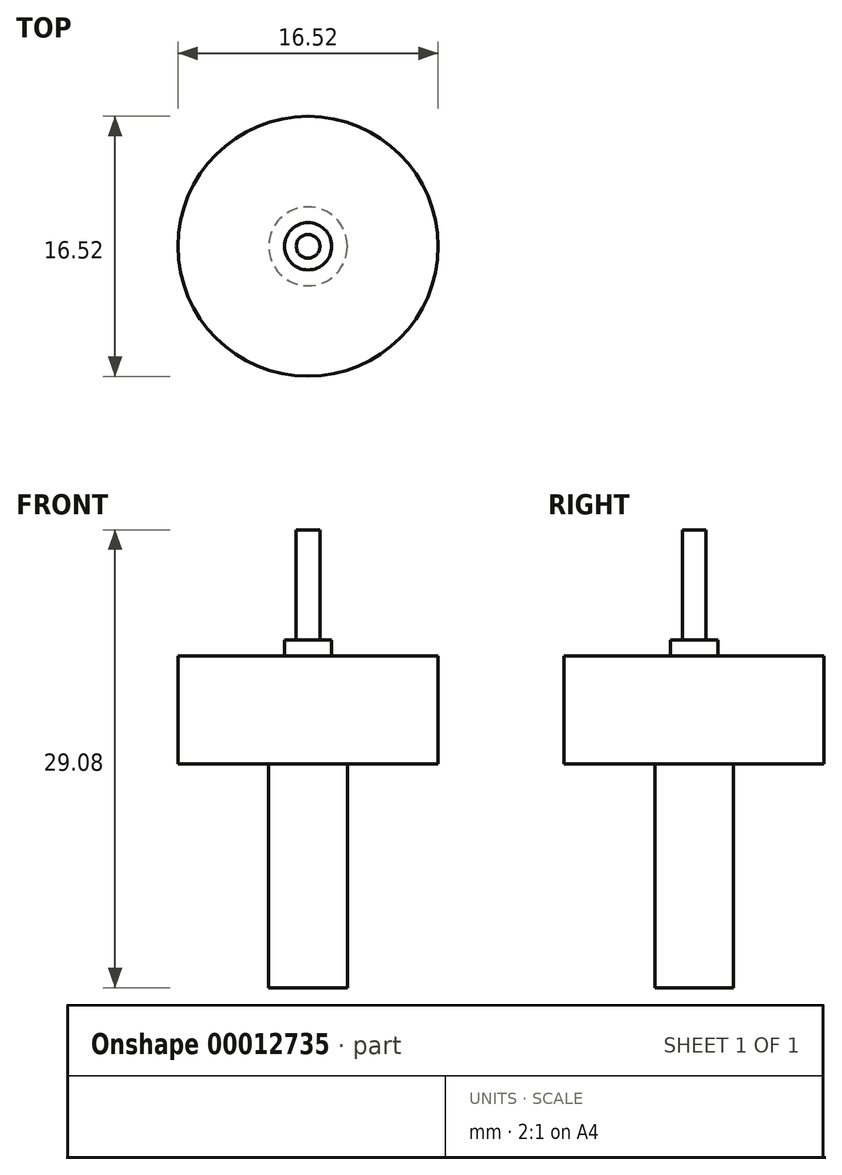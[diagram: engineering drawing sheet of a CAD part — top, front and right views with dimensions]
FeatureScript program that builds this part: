
annotation { "Feature Type Name" : "Feature", "Feature Type Description" : "" }
export const myFeature = defineFeature(function(context is Context, id is Id, definition is map)
    precondition{}
    {
        {
            var Q0;
            Q0=qCreatedBy(makeId("Top.planeOp"),FACE);
            var sketch = newSketch(context, id + "F0", { "sketchPlane" : qUnion([Q0])});
            skCircle(sketch, "E0", {"center": v(0, 0) * mm, "radius": 8.26 * mm});
            skCircle(sketch, "E1", {"center": v(0, 0) * mm, "radius": 2.5 * mm});
            skCircle(sketch, "E2", {"center": v(0, 0) * mm, "radius": 0.75 * mm});
            skSolve(sketch);
        }
        {
            var Q0;
            Q0=makeQuery(id+"F0.imprint","IMPRINT",FACE,{"disambiguationData":[TD([[makeQuery(id+"F0.imprint","IMPRINT",EDGE,{"derivedFrom":sQuery(id+"F0.wireOp",EDGE,"E0")}),1.0]])]});
            var Q1;
            Q1=makeQuery(id+"F0.imprint","IMPRINT",FACE,{"disambiguationData":[TD([[makeQuery(id+"F0.imprint","IMPRINT",EDGE,{"derivedFrom":sQuery(id+"F0.wireOp",EDGE,"E1")}),1.0]])]});
            var Q2;
            Q2=makeQuery(id+"F0.imprint","IMPRINT",FACE,{"disambiguationData":[TD([[makeQuery(id+"F0.imprint","IMPRINT",EDGE,{"derivedFrom":sQuery(id+"F0.wireOp",EDGE,"E2")}),1.0]])]});
            extrude(context, id + "F1", {"entities" : qUnion([Q0, Q1, Q2]), "depth" : 6.86 * mm});
        }
        {
            var Q0;
            Q0=makeQuery(id+"F0.imprint","IMPRINT",FACE,{"disambiguationData":[TD([[makeQuery(id+"F0.imprint","IMPRINT",EDGE,{"derivedFrom":sQuery(id+"F0.wireOp",EDGE,"E1")}),1.0]])]});
            var Q1;
            Q1=makeQuery(id+"F0.imprint","IMPRINT",FACE,{"disambiguationData":[TD([[makeQuery(id+"F0.imprint","IMPRINT",EDGE,{"derivedFrom":sQuery(id+"F0.wireOp",EDGE,"E2")}),1.0]])]});
            extrude(context, id + "F2", {"entities" : qUnion([Q0, Q1]), "operationType" : NewBodyOperationType.ADD, "oppositeDirection" : true, "depth" : 14.22 * mm});
        }
        {
            var Q0;
            Q0=makeQuery(id+"F1.opExtrude","CAP_FACE",FACE,{"disambiguationData":[OSD([sQuery(id+"F0.wireOp",EDGE,"E0")])],"isStart":false});
            var sketch = newSketch(context, id + "F3", { "sketchPlane" : qUnion([Q0])});
            skCircle(sketch, "E3", {"center": v(0, 0) * mm, "radius": 1.5 * mm});
            skCircle(sketch, "E4", {"center": v(0, 0) * mm, "radius": 0.75 * mm});
            skSolve(sketch);
        }
        {
            var Q0;
            Q0=makeQuery(id+"F3.imprint","IMPRINT",FACE,{"disambiguationData":[TD([[makeQuery(id+"F3.imprint","IMPRINT",EDGE,{"derivedFrom":sQuery(id+"F3.wireOp",EDGE,"E4")}),1.0]])]});
            extrude(context, id + "F4", {"entities" : qUnion([Q0]), "operationType" : NewBodyOperationType.ADD, "depth" : 8 * mm});
        }
        {
            var Q0;
            Q0=makeQuery(id+"F3.imprint","IMPRINT",FACE,{"disambiguationData":[TD([[makeQuery(id+"F3.imprint","IMPRINT",EDGE,{"derivedFrom":sQuery(id+"F3.wireOp",EDGE,"E3")}),1.0]])]});
            extrude(context, id + "F5", {"entities" : qUnion([Q0]), "operationType" : NewBodyOperationType.ADD, "depth" : 1 * mm});
        }
    });
